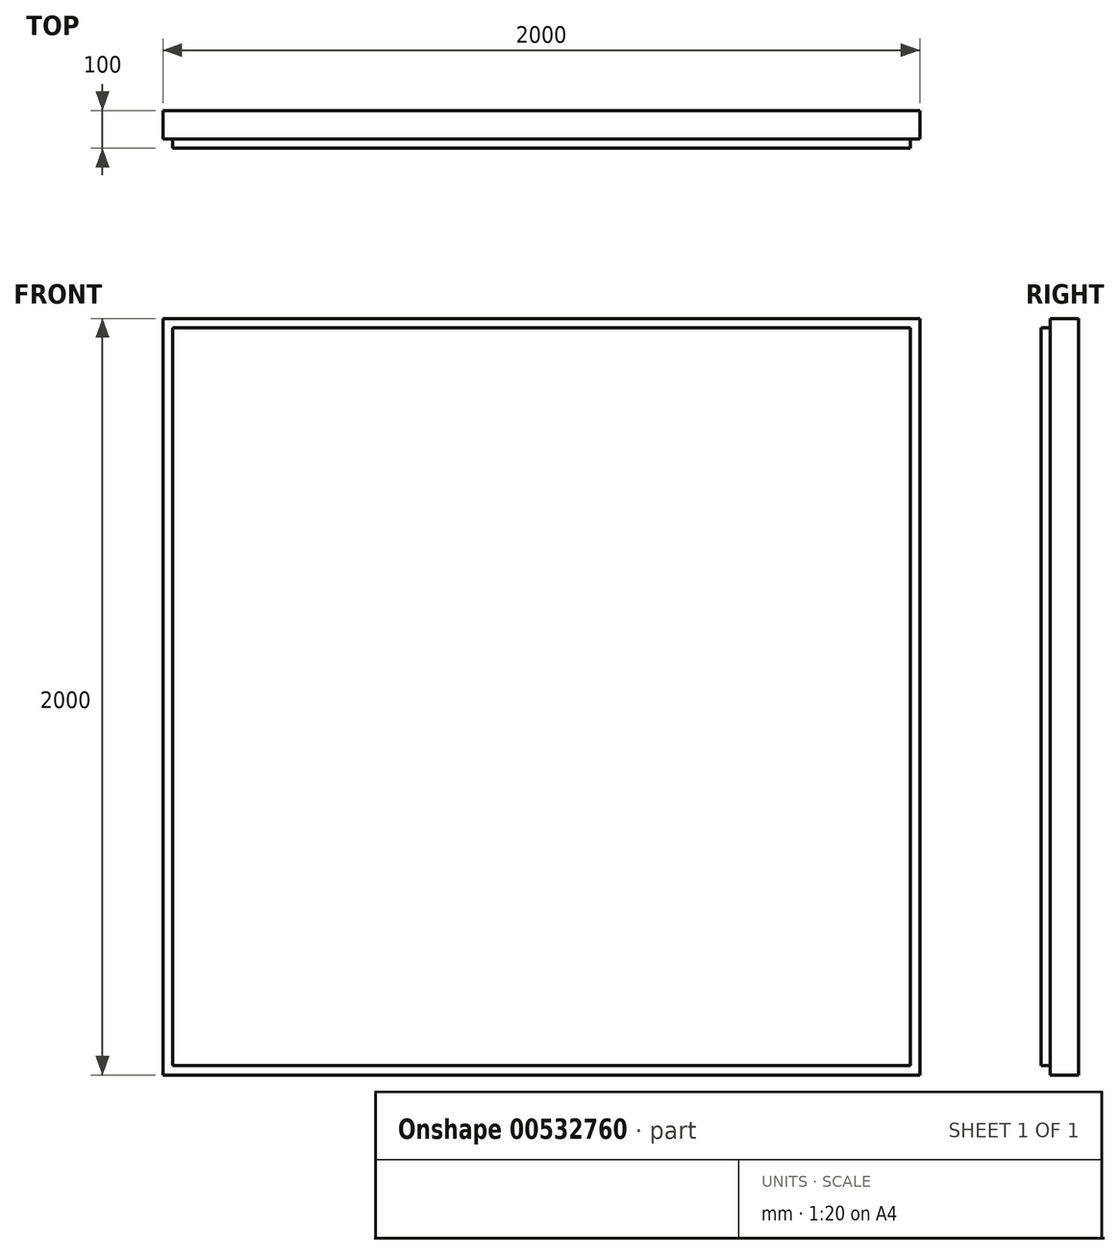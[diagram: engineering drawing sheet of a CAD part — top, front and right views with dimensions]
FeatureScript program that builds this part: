
annotation { "Feature Type Name" : "Feature", "Feature Type Description" : "" }
export const myFeature = defineFeature(function(context is Context, id is Id, definition is map)
    precondition{}
    {
        {
            var Q0;
            Q0=qCreatedBy(makeId("Front.planeOp"),FACE);
            var sketch = newSketch(context, id + "F0", { "sketchPlane" : qUnion([Q0])});
            skLineSegment(sketch, "E0.bottom", {"start": v(0, 0) * mm, "end": v(-2000, 0) * mm});
            skLineSegment(sketch, "E0.top", {"start": v(0, 2000) * mm, "end": v(-2000, 2000) * mm});
            skLineSegment(sketch, "E0.left", {"start": v(0, 0) * mm, "end": v(0, 2000) * mm});
            skLineSegment(sketch, "E0.right", {"start": v(-2000, 0) * mm, "end": v(-2000, 2000) * mm});
            skSolve(sketch);
        }
        {
            var Q0;
            Q0=makeQuery(id+"F0.imprint","IMPRINT",FACE,{"disambiguationData":[TD([[makeQuery(id+"F0.imprint","IMPRINT",EDGE,{"derivedFrom":sQuery(id+"F0.wireOp",EDGE,"E0.bottom")}),-1.0]])]});
            extrude(context, id + "F1", {"entities" : qUnion([Q0]), "oppositeDirection" : true, "depth" : 100 * mm, "offsetDistance" : 25 * mm});
        }
        {
            var Q0;
            Q0=makeQuery(id+"F1.opExtrude","CAP_FACE",FACE,{"disambiguationData":[OSD([sQuery(id+"F0.wireOp",EDGE,"E0.bottom"),sQuery(id+"F0.wireOp",EDGE,"E0.top"),sQuery(id+"F0.wireOp",EDGE,"E0.left"),sQuery(id+"F0.wireOp",EDGE,"E0.right")])],"isStart":true});
            var sketch = newSketch(context, id + "F2", { "sketchPlane" : qUnion([Q0])});
            skLineSegment(sketch, "E1.0", {"start": v(-25, 25) * mm, "end": v(-25, 1975) * mm});
            skLineSegment(sketch, "E1.1", {"start": v(-1975, 25) * mm, "end": v(-25, 25) * mm});
            skLineSegment(sketch, "E1.2", {"start": v(-1975, 1975) * mm, "end": v(-1975, 25) * mm});
            skLineSegment(sketch, "E1.3", {"start": v(-25, 1975) * mm, "end": v(-1975, 1975) * mm});
            skSolve(sketch);
        }
        {
            var Q0;
            Q0=makeQuery(id+"F2.imprint","IMPRINT",FACE,{"disambiguationData":[TD([[makeQuery(id+"F2.imprint","IMPRINT",EDGE,{"derivedFrom":sQuery(id+"F2.wireOp",EDGE,"E1.0")}),-1.0]])]});
            extrude(context, id + "F3", {"entities" : qUnion([Q0]), "operationType" : NewBodyOperationType.REMOVE, "oppositeDirection" : true, "depth" : 25 * mm, "offsetDistance" : 25 * mm});
        }
    });
